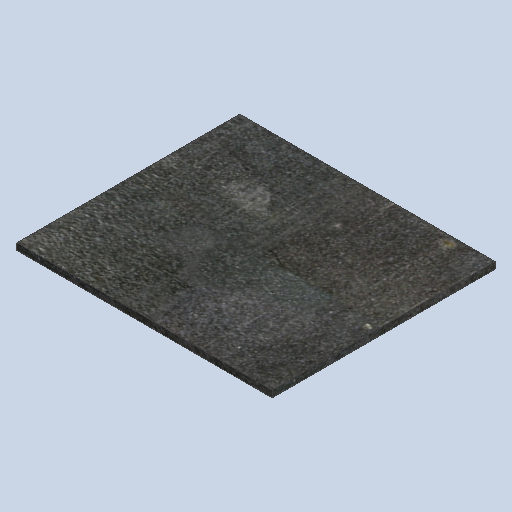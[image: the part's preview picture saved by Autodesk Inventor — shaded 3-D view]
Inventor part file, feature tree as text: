
AUTODESK INVENTOR PART (.ipt)
format: ipt  version: 2024.3 (Build 283343000, 343)  size: 225,792 bytes
history: native  units: mm
features: extrude x1, sketch x1
ambient origin geometry x8: Origin, YZ Plane, XZ Plane, XY Plane, X Axis, Y Axis, Z Axis, Center Point
bodies: Solid1 (feature_tree)
feature tree (2):
  extrude  "Extrusion1"  Depth=114.554mm
  sketch  "Sketch1"  dims[d0=100.0mm d1=114.554mm d2=3.0mm d3=0.0mm]
